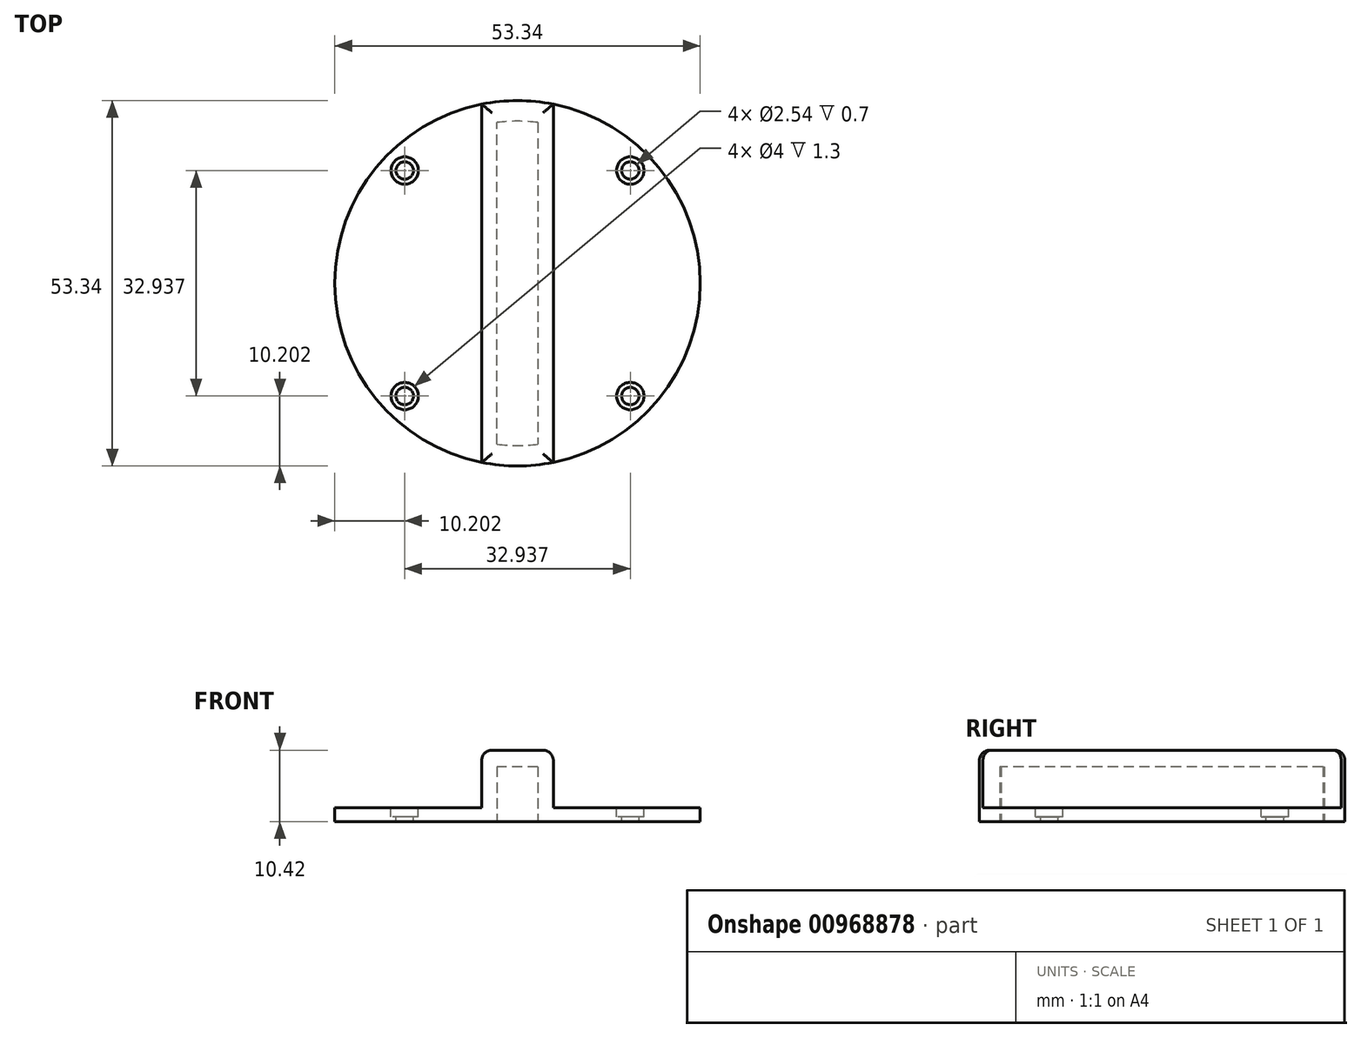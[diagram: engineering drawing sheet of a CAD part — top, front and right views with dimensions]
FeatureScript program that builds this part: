
annotation { "Feature Type Name" : "Feature", "Feature Type Description" : "" }
export const myFeature = defineFeature(function(context is Context, id is Id, definition is map)
    precondition{}
    {
        {
            var Q0;
            Q0=qCreatedBy(makeId("Top.planeOp"),FACE);
            var sketch = newSketch(context, id + "F0", { "sketchPlane" : qUnion([Q0])});
            skCircle(sketch, "E0", {"center": v(0, 0) * mm, "radius": 26.67 * mm});
            skSolve(sketch);
        }
        {
            var Q0;
            Q0=makeQuery(id+"F0.imprint","IMPRINT",FACE,{"disambiguationData":[TD([[makeQuery(id+"F0.imprint","IMPRINT",EDGE,{"derivedFrom":sQuery(id+"F0.wireOp",EDGE,"E0")}),1.0]])]});
            var Q1;
            Q1 = qSketchRegion(id + "F0", true);
            extrude(context, id + "F1", {"entities" : qUnion([Q0, Q1]), "depth" : 2 * mm, "offsetDistance" : 25 * mm});
        }
        {
            var Q0;
            Q0=makeQuery(id+"F1.opExtrude","CAP_FACE",FACE,{"disambiguationData":[OSD([sQuery(id+"F0.wireOp",EDGE,"E0")])],"isStart":false});
            var sketch = newSketch(context, id + "F2", { "sketchPlane" : qUnion([Q0])});
            skCircle(sketch, "E1", {"center": v(0, 0) * mm, "radius": 23.29 * mm});
            skSolve(sketch);
        }
        {
            var Q0;
            Q0=makeQuery(id+"F2.imprint","IMPRINT",FACE,{"disambiguationData":[TD([[makeQuery(id+"F2.imprint","IMPRINT",EDGE,{"derivedFrom":sQuery(id+"F2.wireOp",EDGE,"E1")}),1.0]])]});
            var sketch = newSketch(context, id + "F3", { "sketchPlane" : qUnion([Q0])});
            skLineSegment(sketch, "E2", {"start": v(0, 0) * mm, "end": v(-16.47, 16.47) * mm});
            skSolve(sketch);
        }
        {
            var Q0;
            Q0=makeQuery(id+"F1.opExtrude","CAP_FACE",FACE,{"disambiguationData":[OSD([sQuery(id+"F0.wireOp",EDGE,"E0")])],"isStart":false});
            var sketch = newSketch(context, id + "F4", { "sketchPlane" : qUnion([Q0])});
            skLineSegment(sketch, "E3", {"start": v(-5.23, 26.15) * mm, "end": v(-5.23, -26.15) * mm});
            skArc(sketch, "E4", {"start": v(5.23, 26.15) * mm, "mid": v(0, 26.67) * mm, "end": v(-5.23, 26.15) * mm});
            skLineSegment(sketch, "E5", {"start": v(5.23, 26.15) * mm, "end": v(5.23, -26.15) * mm});
            skArc(sketch, "E6", {"start": v(-5.23, -26.15) * mm, "mid": v(0, -26.67) * mm, "end": v(5.23, -26.15) * mm});
            skSolve(sketch);
        }
        {
            var Q0;
            Q0 = qSketchRegion(id + "F4", true);
            extrude(context, id + "F5", {"entities" : qUnion([Q0]), "operationType" : NewBodyOperationType.ADD, "depth" : 8.42 * mm, "offsetDistance" : 25 * mm});
        }
        {
            var Q0;
            Q0=makeQuery(id+"F5.opExtrude","CAP_FACE",FACE,{"disambiguationData":[OSD([sQuery(id+"F4.wireOp",EDGE,"E3"),sQuery(id+"F4.wireOp",EDGE,"E4"),sQuery(id+"F4.wireOp",EDGE,"E5"),sQuery(id+"F4.wireOp",EDGE,"E6")])],"isStart":false});
            fillet(context, id + "F6", {"entities" : qUnion([Q0]), "radius" : 1.5 * mm, "tangentPropagation" : true, "allowEdgeOverflow" : false});
        }
        {
            var Q0;
            Q0=makeQuery(id+"F1.opExtrude","CAP_FACE",FACE,{"disambiguationData":[OSD([sQuery(id+"F0.wireOp",EDGE,"E0")])],"isStart":true});
            var sketch = newSketch(context, id + "F7", { "sketchPlane" : qUnion([Q0])});
            skLineSegment(sketch, "E7", {"start": v(-3, 23.48) * mm, "end": v(-3, -23.48) * mm});
            skLineSegment(sketch, "E8", {"start": v(3, -23.48) * mm, "end": v(3, 23.48) * mm});
            skArc(sketch, "E9", {"start": v(3, 23.48) * mm, "mid": v(0, 23.67) * mm, "end": v(-3, 23.48) * mm});
            skArc(sketch, "E10", {"start": v(-3, -23.48) * mm, "mid": v(0, -23.67) * mm, "end": v(3, -23.48) * mm});
            skSolve(sketch);
        }
        {
            var Q0;
            Q0 = qSketchRegion(id + "F7", true);
            extrude(context, id + "F8", {"entities" : qUnion([Q0]), "operationType" : NewBodyOperationType.REMOVE, "oppositeDirection" : true, "depth" : 8 * mm, "offsetDistance" : 25 * mm});
        }
        {
            var Q0;
            Q0=makeQuery(id+"F3.imprint","IMPRINT",FACE,{"disambiguationData":[TD([[makeQuery(id+"F3.imprint","IMPRINT",EDGE,{"derivedFrom":makeQuery(id+"F2.imprint","IMPRINT",EDGE,{"derivedFrom":sQuery(id+"F2.wireOp",EDGE,"E1")})}),1.0]])]});
            var sketch = newSketch(context, id + "F9", { "sketchPlane" : qUnion([Q0])});
            skCircle(sketch, "E11", {"center": v(-16.47, 16.47) * mm, "radius": 1.27 * mm});
            skCircle(sketch, "E12.1.0", {"center": v(-16.47, -16.47) * mm, "radius": 1.27 * mm});
            skCircle(sketch, "E12.2.0", {"center": v(16.47, -16.47) * mm, "radius": 1.27 * mm});
            skCircle(sketch, "E12.3.0", {"center": v(16.47, 16.47) * mm, "radius": 1.27 * mm});
            skPoint(sketch, "E12.center", {"position": v(0, 0) * mm});
            skSolve(sketch);
        }
        {
            var Q0;
            Q0=makeQuery(id+"F3.imprint","IMPRINT",FACE,{"disambiguationData":[TD([[makeQuery(id+"F3.imprint","IMPRINT",EDGE,{"derivedFrom":makeQuery(id+"F2.imprint","IMPRINT",EDGE,{"derivedFrom":sQuery(id+"F2.wireOp",EDGE,"E1")})}),1.0]])]});
            var sketch = newSketch(context, id + "F10", { "sketchPlane" : qUnion([Q0])});
            skCircle(sketch, "E13", {"center": v(-16.47, 16.47) * mm, "radius": 2 * mm});
            skCircle(sketch, "E14.1.0", {"center": v(-16.47, -16.47) * mm, "radius": 2 * mm});
            skCircle(sketch, "E14.2.0", {"center": v(16.47, -16.47) * mm, "radius": 2 * mm});
            skCircle(sketch, "E14.3.0", {"center": v(16.47, 16.47) * mm, "radius": 2 * mm});
            skPoint(sketch, "E14.center", {"position": v(0, 0) * mm});
            skSolve(sketch);
        }
        {
            var Q0;
            Q0 = qSketchRegion(id + "F9", true);
            extrude(context, id + "F11", {"entities" : qUnion([Q0]), "operationType" : NewBodyOperationType.REMOVE, "oppositeDirection" : true, "depth" : 2 * mm, "offsetDistance" : 25 * mm});
        }
        {
            var Q0;
            Q0 = qSketchRegion(id + "F10", true);
            extrude(context, id + "F12", {"entities" : qUnion([Q0]), "operationType" : NewBodyOperationType.REMOVE, "oppositeDirection" : true, "depth" : 1.3 * mm, "offsetDistance" : 25 * mm});
        }
    });
